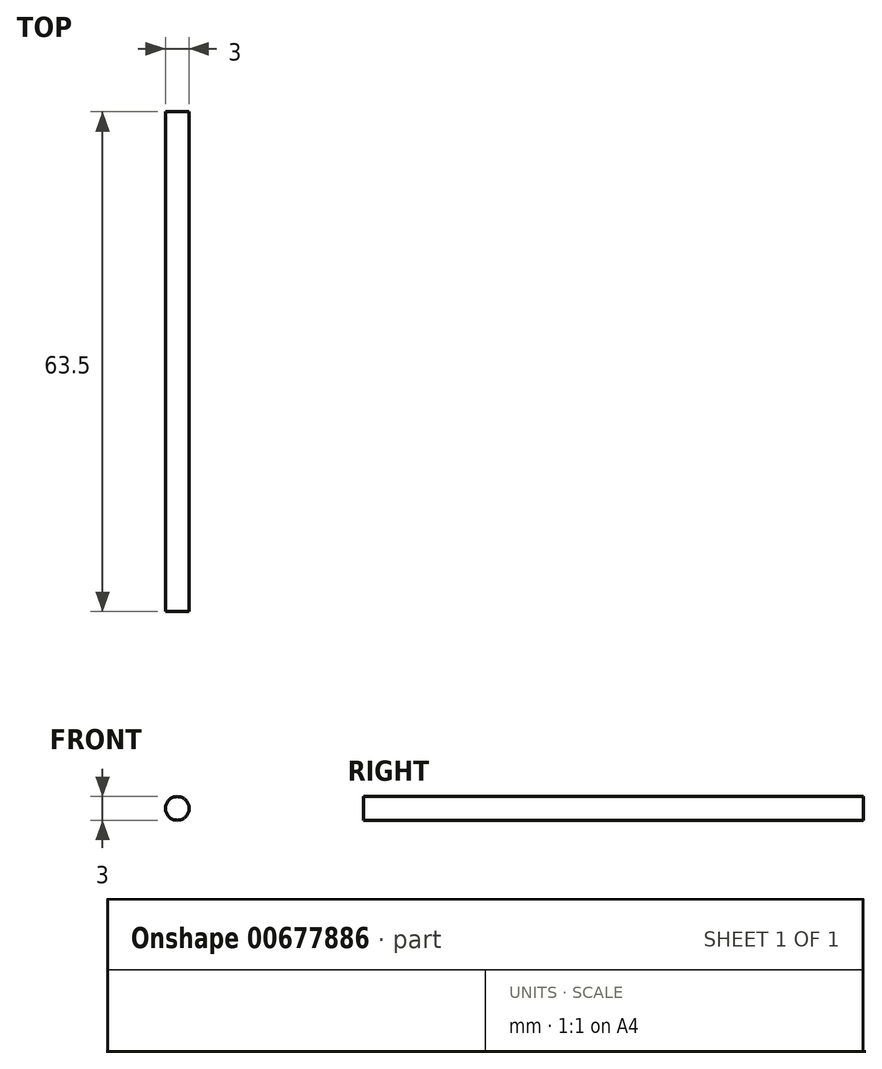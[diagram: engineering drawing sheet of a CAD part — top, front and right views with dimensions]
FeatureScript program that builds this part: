
annotation { "Feature Type Name" : "Feature", "Feature Type Description" : "" }
export const myFeature = defineFeature(function(context is Context, id is Id, definition is map)
    precondition{}
    {
        {
            var Q0;
            Q0=qCreatedBy(makeId("Front.planeOp"),FACE);
            var sketch = newSketch(context, id + "F0", { "sketchPlane" : qUnion([Q0])});
            skCircle(sketch, "E0", {"center": v(0, 0) * mm, "radius": 1.5 * mm});
            skSolve(sketch);
        }
        {
            var Q0;
            Q0=makeQuery(id+"F0.imprint","IMPRINT",FACE,{"disambiguationData":[TD([[makeQuery(id+"F0.imprint","IMPRINT",EDGE,{"derivedFrom":sQuery(id+"F0.wireOp",EDGE,"E0")}),1.0]])]});
            extrude(context, id + "F1", {"entities" : qUnion([Q0]), "oppositeDirection" : true, "depth" : 63.5 * mm, "offsetDistance" : 25 * mm});
        }
    });
